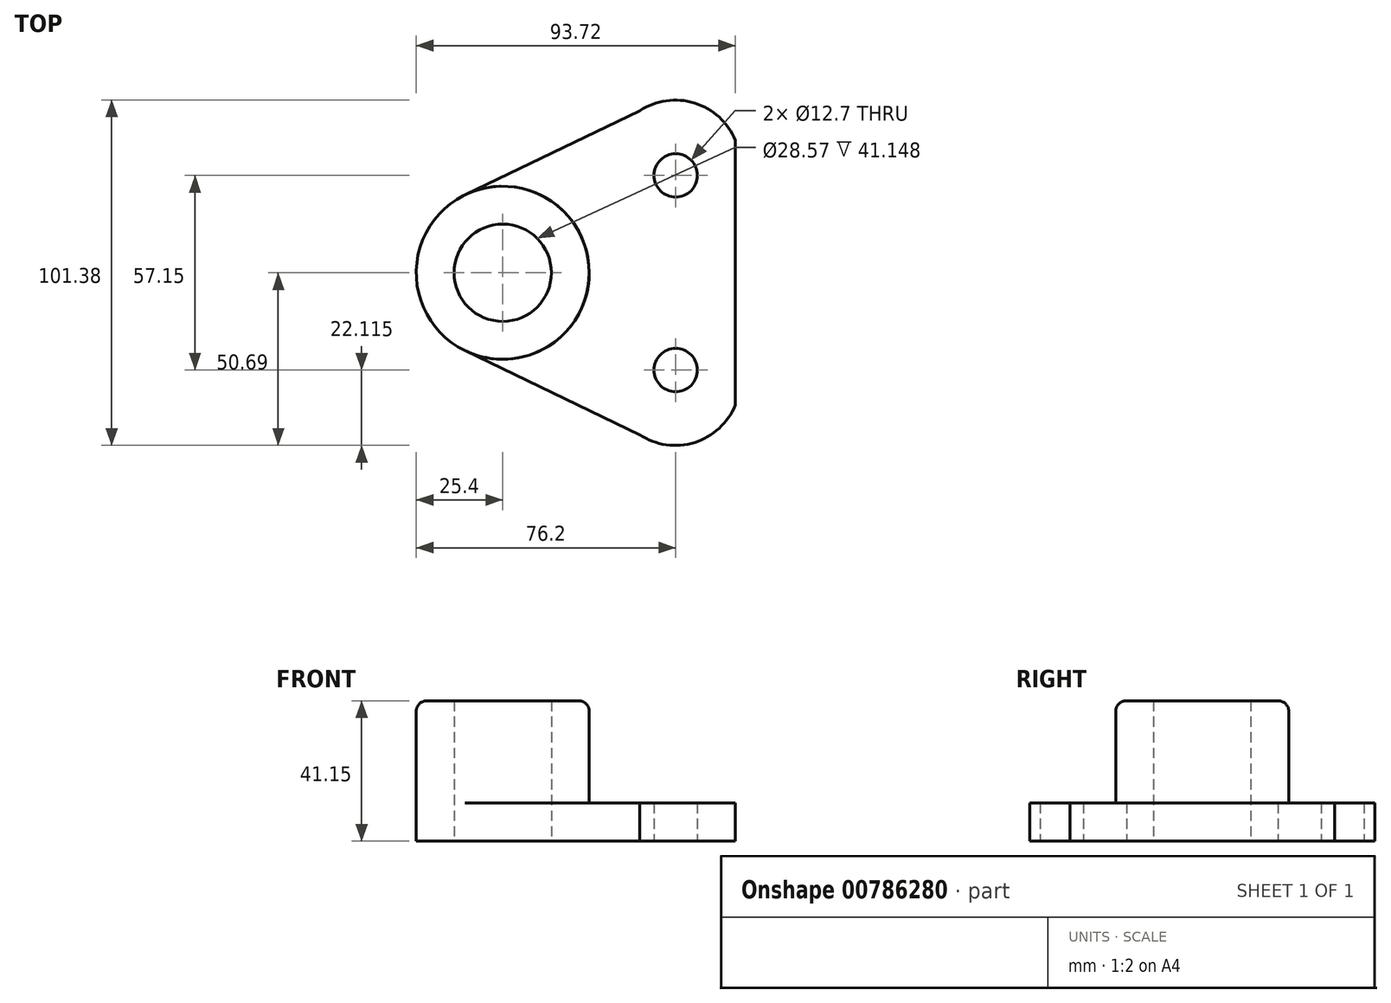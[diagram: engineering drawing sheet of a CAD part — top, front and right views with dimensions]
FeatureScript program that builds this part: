
annotation { "Feature Type Name" : "Feature", "Feature Type Description" : "" }
export const myFeature = defineFeature(function(context is Context, id is Id, definition is map)
    precondition{}
    {
        {
            var Q0;
            Q0=qCreatedBy(makeId("Top.planeOp"),FACE);
            var sketch = newSketch(context, id + "F0", { "sketchPlane" : qUnion([Q0])});
            skCircle(sketch, "E0", {"center": v(0, 0) * mm, "radius": 14.29 * mm});
            skCircle(sketch, "E1", {"center": v(0, 0) * mm, "radius": 25.4 * mm});
            skLineSegment(sketch, "E2", {"start": v(0, 0) * mm, "end": v(68.32, 0) * mm, "construction": true});
            skCircle(sketch, "E3", {"center": v(50.8, 28.57) * mm, "radius": 6.35 * mm});
            skCircle(sketch, "E4.MirrorC", {"center": v(50.8, -28.57) * mm, "radius": 6.35 * mm});
            skLineSegment(sketch, "E5", {"start": v(-11.02, 22.89) * mm, "end": v(40.26, 47.57) * mm});
            skLineSegment(sketch, "E6.MirrorCS", {"start": v(-11.02, -22.89) * mm, "end": v(40.26, -47.57) * mm});
            skLineSegment(sketch, "E7", {"start": v(68.32, 0) * mm, "end": v(68.32, 38.87) * mm});
            skLineSegment(sketch, "E8.MirrorCS", {"start": v(68.32, 0) * mm, "end": v(68.32, -38.87) * mm});
            skArc(sketch, "E9", {"start": v(68.32, 38.87) * mm, "mid": v(56.34, 49.83) * mm, "end": v(40.26, 47.57) * mm});
            skArc(sketch, "E10.MirrorCS", {"start": v(68.32, -38.87) * mm, "mid": v(56.34, -49.83) * mm, "end": v(40.26, -47.57) * mm});
            skSolve(sketch);
        }
        {
            var Q0;
            Q0=makeQuery(id+"F0.imprint","IMPRINT",FACE,{"disambiguationData":[TD([[makeQuery(id+"F0.imprint","IMPRINT",EDGE,{"derivedFrom":sQuery(id+"F0.wireOp",EDGE,"E3")}),-1.0]])]});
            extrude(context, id + "F1", {"entities" : qUnion([Q0]), "depth" : 11.18 * mm, "offsetDistance" : 25.4 * mm});
        }
        {
            var Q0;
            Q0=makeQuery(id+"F0.imprint","IMPRINT",FACE,{"disambiguationData":[TD([[makeQuery(id+"F0.imprint","IMPRINT",EDGE,{"derivedFrom":sQuery(id+"F0.wireOp",EDGE,"E0")}),-1.0]])]});
            extrude(context, id + "F2", {"entities" : qUnion([Q0]), "operationType" : NewBodyOperationType.ADD, "depth" : 41.15 * mm, "offsetDistance" : 25.4 * mm});
        }
        {
            var Q0;
            Q0=makeQuery(id+"F2.opExtrude","CAP_EDGE",EDGE,{"disambiguationData":[OSD([sQuery(id+"F0.wireOp",EDGE,"E1")])],"isStart":false});
            fillet(context, id + "F3", {"entities" : qUnion([Q0]), "radius" : 3.05 * mm, "tangentPropagation" : true, "allowEdgeOverflow" : false});
        }
        {
            var Q0;
            Q0=makeQuery(id+"F1.opExtrude","CAP_FACE",FACE,{"disambiguationData":[OSD([sQuery(id+"F0.wireOp",EDGE,"E1"),sQuery(id+"F0.wireOp",EDGE,"E3"),sQuery(id+"F0.wireOp",EDGE,"E4.MirrorC"),sQuery(id+"F0.wireOp",EDGE,"E5"),sQuery(id+"F0.wireOp",EDGE,"E6.MirrorCS"),sQuery(id+"F0.wireOp",EDGE,"E7"),sQuery(id+"F0.wireOp",EDGE,"E8.MirrorCS"),sQuery(id+"F0.wireOp",EDGE,"E9"),sQuery(id+"F0.wireOp",EDGE,"E10.MirrorCS")])],"isStart":false});
            cPlane(context, id + "F4", {"entities" : qUnion([Q0]), "cplaneType" : CPlaneType.OFFSET, "offset" : 25.4 * mm, "width" : 152.4 * mm, "height" : 152.4 * mm});
        }
    });
